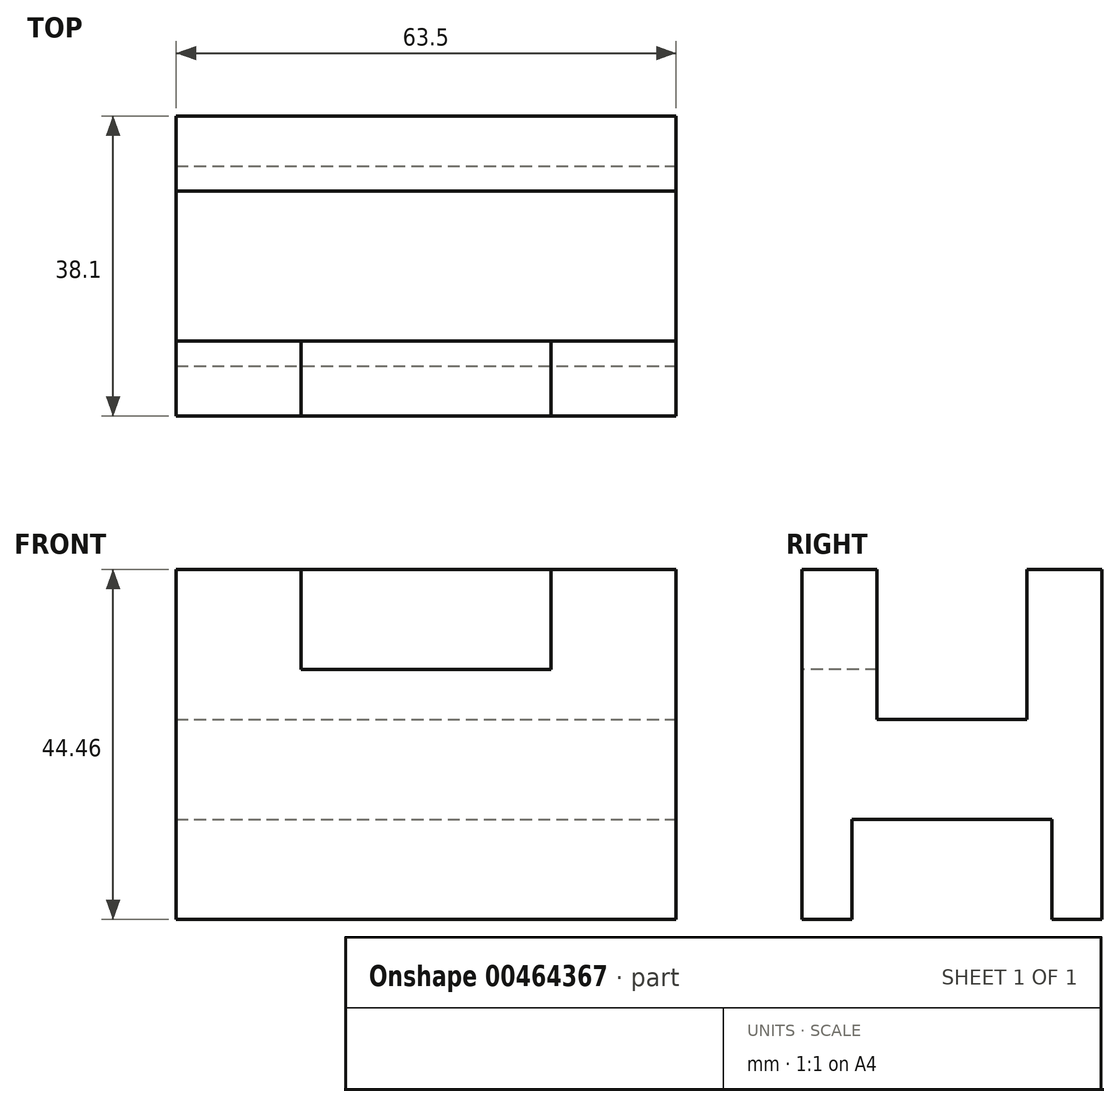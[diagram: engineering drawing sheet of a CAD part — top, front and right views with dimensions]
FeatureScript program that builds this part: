
annotation { "Feature Type Name" : "Feature", "Feature Type Description" : "" }
export const myFeature = defineFeature(function(context is Context, id is Id, definition is map)
    precondition{}
    {
        {
            var Q0;
            Q0=qCreatedBy(makeId("Front.planeOp"),FACE);
            var sketch = newSketch(context, id + "F0", { "sketchPlane" : qUnion([Q0])});
            skLineSegment(sketch, "E0.bottom", {"start": v(31.75, 22.23) * mm, "end": v(-31.75, 22.23) * mm});
            skLineSegment(sketch, "E0.top", {"start": v(31.75, -22.23) * mm, "end": v(-31.75, -22.23) * mm});
            skLineSegment(sketch, "E0.left", {"start": v(31.75, 22.23) * mm, "end": v(31.75, -22.23) * mm});
            skLineSegment(sketch, "E0.right", {"start": v(-31.75, 22.23) * mm, "end": v(-31.75, -22.23) * mm});
            skPoint(sketch, "E0.middle", {"position": v(0, 0) * mm});
            skSolve(sketch);
        }
        {
            var Q0;
            Q0 = qSketchRegion(id + "F0", true);
            extrude(context, id + "F1", {"entities" : qUnion([Q0]), "depth" : 38.1 * mm});
        }
        {
            var Q0;
            Q0=makeQuery(id+"F1.opExtrude","CAP_FACE",FACE,{"disambiguationData":[OSD([sQuery(id+"F0.wireOp",EDGE,"E0.bottom"),sQuery(id+"F0.wireOp",EDGE,"E0.top"),sQuery(id+"F0.wireOp",EDGE,"E0.left"),sQuery(id+"F0.wireOp",EDGE,"E0.right")])],"isStart":false});
            var sketch = newSketch(context, id + "F2", { "sketchPlane" : qUnion([Q0])});
            skLineSegment(sketch, "E1.bottom", {"start": v(-15.87, 22.23) * mm, "end": v(15.87, 22.23) * mm});
            skLineSegment(sketch, "E1.top", {"start": v(-15.87, 9.53) * mm, "end": v(15.88, 9.53) * mm});
            skLineSegment(sketch, "E1.left", {"start": v(-15.88, 22.23) * mm, "end": v(-15.88, 9.53) * mm});
            skLineSegment(sketch, "E1.right", {"start": v(15.88, 22.23) * mm, "end": v(15.88, 9.53) * mm});
            skSolve(sketch);
        }
        {
            var Q0;
            Q0 = qSketchRegion(id + "F2", true);
            extrude(context, id + "F3", {"entities" : qUnion([Q0]), "operationType" : NewBodyOperationType.REMOVE, "oppositeDirection" : true, "depth" : 9.52 * mm});
        }
        {
            var Q0;
            Q0=makeQuery(id+"F1.opExtrude","SWEPT_FACE",FACE,{"disambiguationData":[OSD([sQuery(id+"F0.wireOp",EDGE,"E0.bottom")])]});
            var sketch = newSketch(context, id + "F4", { "sketchPlane" : qUnion([Q0])});
            skLineSegment(sketch, "E2.bottom", {"start": v(-31.75, -9.53) * mm, "end": v(31.75, -9.53) * mm});
            skLineSegment(sketch, "E2.top", {"start": v(-31.75, -28.58) * mm, "end": v(31.75, -28.57) * mm});
            skLineSegment(sketch, "E2.left", {"start": v(-31.75, -9.53) * mm, "end": v(-31.75, -28.58) * mm});
            skLineSegment(sketch, "E2.right", {"start": v(31.75, -9.52) * mm, "end": v(31.75, -28.57) * mm});
            skSolve(sketch);
        }
        {
            var Q0;
            Q0 = qSketchRegion(id + "F4", true);
            extrude(context, id + "F5", {"entities" : qUnion([Q0]), "operationType" : NewBodyOperationType.REMOVE, "oppositeDirection" : true, "depth" : 19.05 * mm});
        }
        {
            var Q0;
            Q0=makeQuery(id+"F1.opExtrude","SWEPT_FACE",FACE,{"disambiguationData":[OSD([sQuery(id+"F0.wireOp",EDGE,"E0.left")])]});
            var sketch = newSketch(context, id + "F6", { "sketchPlane" : qUnion([Q0])});
            skLineSegment(sketch, "E3.bottom", {"start": v(-6.35, -22.23) * mm, "end": v(-31.75, -22.23) * mm});
            skLineSegment(sketch, "E3.top", {"start": v(-6.35, -9.53) * mm, "end": v(-31.75, -9.53) * mm});
            skLineSegment(sketch, "E3.left", {"start": v(-6.35, -22.23) * mm, "end": v(-6.35, -9.53) * mm});
            skLineSegment(sketch, "E3.right", {"start": v(-31.75, -22.23) * mm, "end": v(-31.75, -9.53) * mm});
            skSolve(sketch);
        }
        {
            var Q0;
            Q0 = qSketchRegion(id + "F6", true);
            extrude(context, id + "F7", {"entities" : qUnion([Q0]), "operationType" : NewBodyOperationType.REMOVE, "endBound" : BoundingType.THROUGH_ALL, "oppositeDirection" : true, "depth" : 25.4 * mm});
        }
    });
